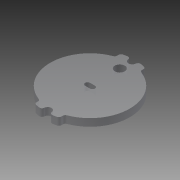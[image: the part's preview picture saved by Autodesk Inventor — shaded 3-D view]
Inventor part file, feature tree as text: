
AUTODESK INVENTOR PART (.ipt)
format: ipt  version: 2013 SP1 (Build 170176100, 176)  size: 123,904 bytes
history: native  units: mm
features: extrude x1, sketch x1
ambient origin geometry x8: Origin, YZ Plane, XZ Plane, XY Plane, X Axis, Y Axis, Z Axis, Center Point
feature tree (2):
  extrude  "Extrusion4"  Depth=4.0mm
  sketch  "Sketch1"  dims[d0=31.75mm d6=4.0mm d11=10.0mm d12=5.0mm d15=36.0mm d16=1.0mm d17=16.0mm d18=16.0mm d19=18.0mm d20=18.0mm d21=10.0mm d22=10.0mm d25=3.0mm d28=3.0mm d29=1.0mm d34=12.0mm d35=2.0mm d36=2.0mm d37=3.0mm d38=0.0mm]
